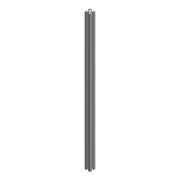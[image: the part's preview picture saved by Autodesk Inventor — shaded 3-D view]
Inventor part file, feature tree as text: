
AUTODESK INVENTOR PART (.ipt)
format: ipt  version: 2019 (Build 230136000, 136)  size: 152,576 bytes
history: native  units: mm
features: other x4, extrude x1, sketch x1, reference x1
ambient origin geometry x8: Origin, YZ Plane, XZ Plane, XY Plane, X Axis, Y Axis, Z Axis, Center Point
bodies: Body1 (feature_tree)
feature tree (7):
  other  "솔리드1"
  extrude  "돌출1"  Depth=500.0mm TaperAngle=0.0deg
  sketch  "스케치1"
  reference  "참조1"
  other  "<userpath>\Documents\Inventor\Projects\2019_CapstoneDesign\Body.iam"
  other  "Body.iam"
  other  "Propile_202070:2"
